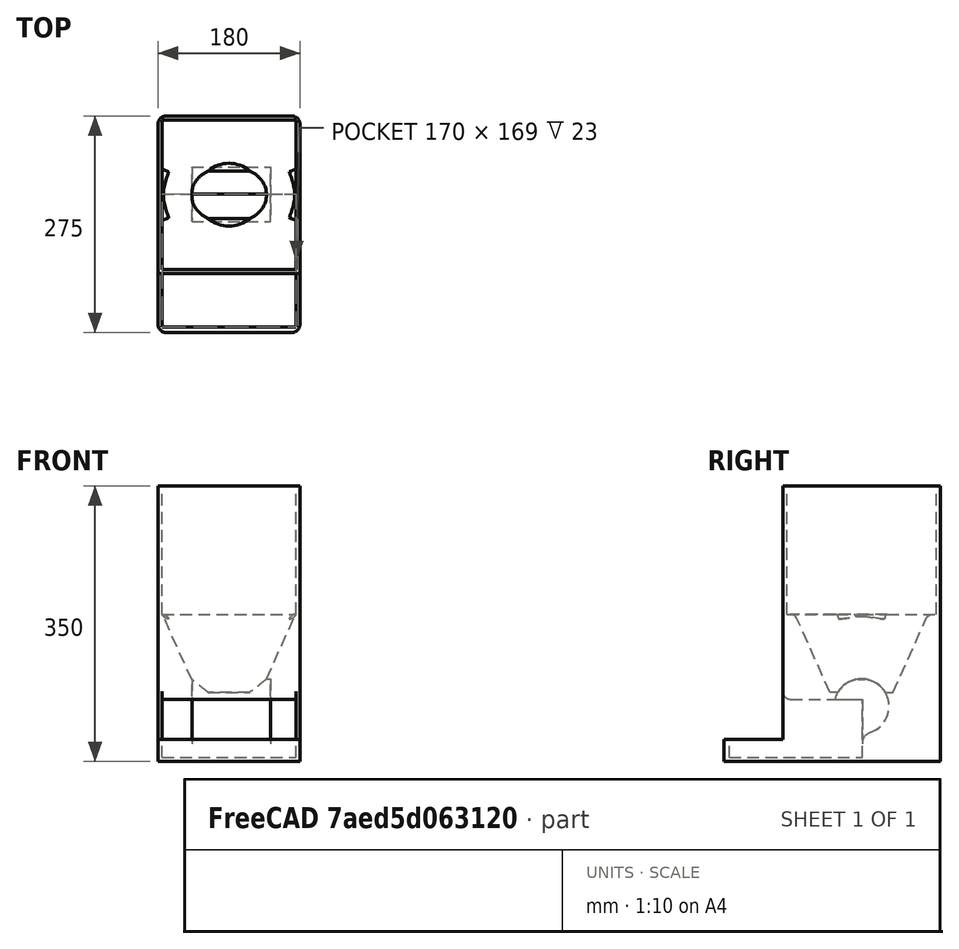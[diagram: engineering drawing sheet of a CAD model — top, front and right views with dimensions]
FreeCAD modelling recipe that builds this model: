
FCSTD DOCUMENT  (FreeCAD 0.16R6706 (Git))
Label: Petbuddy3
License: All rights reserved
LicenseURL: http://en.wikipedia.org/wiki/All_rights_reserved
objects: Part::Fillet×7, Part::Box×4, Part::Cut×4, Part::Cone×1, Part::Cylinder×1, Part::MultiFuse×1
note: 18 computed .brp shape members not serialized (recipe doc carries the construction recipe); baked Part::Feature solids carry a one-line shape summary decoded from their .brp

FEATURE [Part::Box] Box  label="Cube"
  Height = 350
  Length = 180
  Width = 200
FEATURE [Part::Cone] Cone
  Angle = 360
  Height = 100
  Placement = pos=(90,100,88) rot=(0,0,1;0rad)
  Radius1 = 40
  Radius2 = 85
FEATURE [Part::Cut] Cut
  Base = -> Box
  Tool = -> Cone
FEATURE [Part::Box] Box001  label="Cube001"
  Height = 166
  Length = 170
  Placement = pos=(5,5,187) rot=(0,0,1;0rad)
  Width = 190
FEATURE [Part::Cut] Cut001
  Base = -> Cut
  Tool = -> Box001
FEATURE [Part::Cylinder] Cylinder
  Angle = 360
  Height = 100
  Placement = pos=(43,100,70) rot=(0,1,0;1.5708rad)
  Radius = 35
FEATURE [Part::Box] Box002  label="Cube002"
  Height = 28
  Length = 180
  Placement = pos=(0,-75,0) rot=(0,0,1;0rad)
  Width = 80
FEATURE [Part::MultiFuse] Fusion
  Shapes = -> [Box002,Cut001]
FEATURE [Part::Box] Box003  label="Cube003"
  Height = 74
  Length = 170
  Placement = pos=(5,-68,5) rot=(0,0,1;0rad)
  Width = 169
FEATURE [Part::Cut] Cut002
  Base = -> Fusion
  Tool = -> Box003
FEATURE [Part::Cut] Cut003
  Base = -> Cut002
  Tool = -> Cylinder
FEATURE [Part::Fillet] Fillet
  Base = -> Cut003
  Edges = 1 edges r=10: [Edge43]
FEATURE [Part::Fillet] Fillet001
  Base = -> Fillet
  Edges = 1 edges r=10: [Edge7]
FEATURE [Part::Fillet] Fillet002
  Base = -> Fillet001
  Edges = 1 edges r=10: [Edge68]
FEATURE [Part::Fillet] Fillet003
  Base = -> Fillet002
  Edges = 1 edges r=10: [Edge14]
FEATURE [Part::Fillet] Fillet004
  Base = -> Fillet003
  Edges = 1 edges r=10: [Edge90]
FEATURE [Part::Fillet] Fillet005
  Base = -> Fillet004
  Edges = 1 edges r=15: [Edge70]
FEATURE [Part::Fillet] Fillet006
  Base = -> Fillet005
  Edges = 1 edges r=10: [Edge23]
